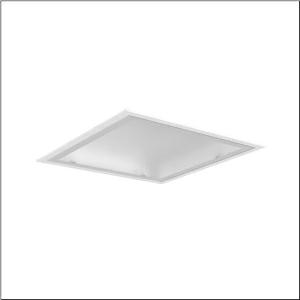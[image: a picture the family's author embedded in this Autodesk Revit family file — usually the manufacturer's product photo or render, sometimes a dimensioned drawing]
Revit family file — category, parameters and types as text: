
# Revit family: mira_11_51fr127a471a
name_source: partatom
category: Lighting Fixtures
units: mm (PartAtom-declared; Revit-internal decimal feet)

## family parameters
Cut with Voids When Loaded = No
Host = Face
Light Source = No
Part Type = Normal
Room Calculation Point = No
Round Connector Dimension = Use Diameter
Shared = No

## types (1)
- Mira 11 (1 x LED, 7290 lm, 66 W, 4000K)
    Apparent Load = 66 VA
    CIE Flux Codes = 51 82 97 100 100
    Color Rendering = 80
    Color Temperature = 4000K
    Default Elevation = 1800 mm
    Description = Mira 11, clean room luminaire, primary light control with reflector, primary optical cover: cover, of toughened safety glass, light emission: direct distribution, primary light characteristic: symmetric, installation type: recessed, LED, rated luminous flux: 7.290lm, luminous efficacy: 111lm/W, light colour: 840, colour temperature: 4000K, control gear: ON/OFF, with terminal, 3-pole, max. 2.5mm², mains connection: 230V, AC, 50/60Hz, rated input power: 66W, luminaire housing, of sheet steel, coated, pure white (RAL 9010), with concealed magnets, module: M625, length: 623mm, width: 623mm, height: 90mm, protection rating (complete): IP65, insulation class (complete): insulation class I (protective earthing), certification: CE, UKCA, permissible operating ambient temperature: -5..+40°C, standard: EN 50419, packaging unit: 1 piece
    Height = 0 mm  [stored 0 ft]
    Lamp = 1 x LED
    Lamp Light Flux = 7290 lm
    Lamp Power = 66 W
    Lamp count = 1
    Length = 625 mm
    Luminous efficacy = 110 lm/W
    Manufacturer = Siteco
    ModVariant = No
    Model = 51FR127A471A
    Mounting Place = Ceiling
    Mounting Type = Recessed
    Number of Poles = 1
    OnlyDefault = Yes
    Power Factor = 1
    Product Name = Mira 11
    Product group = clean room luminaire | ceiling recessed
    ProductGroupID = 402
    Protection Class = Protection class I
    Protection Degree = IP 65
    RLX_Detail_Level = 1
    RLX_Emergency_Light_Flux = 0 lm
    RLX_Emergency_Type = 0
    RLX_Emergency_Type_DB = No
    RlxData = <blob elided: 19229 chars, md5=ef5cf52b>
    Socket = socket
    Standby Power = 0 W
    System Light Flux = 7290 lm
    System Power = 66 W
    Type Comments = Product without accessories
    Type Image = l_1006636.jpg
    URL = http://relux.com
    VarID = ---
    Voltage = 0 V
    Weight = 0.00 kg
    Width = 625 mm

note: [stored X ft] marks values corroborated as IEEE doubles in the binary element streams (Revit-internal decimal feet)

## geometry (parser evidence)
native form markers: Blend x4, Sweep x9
no freeform markers — native parametric forms only
